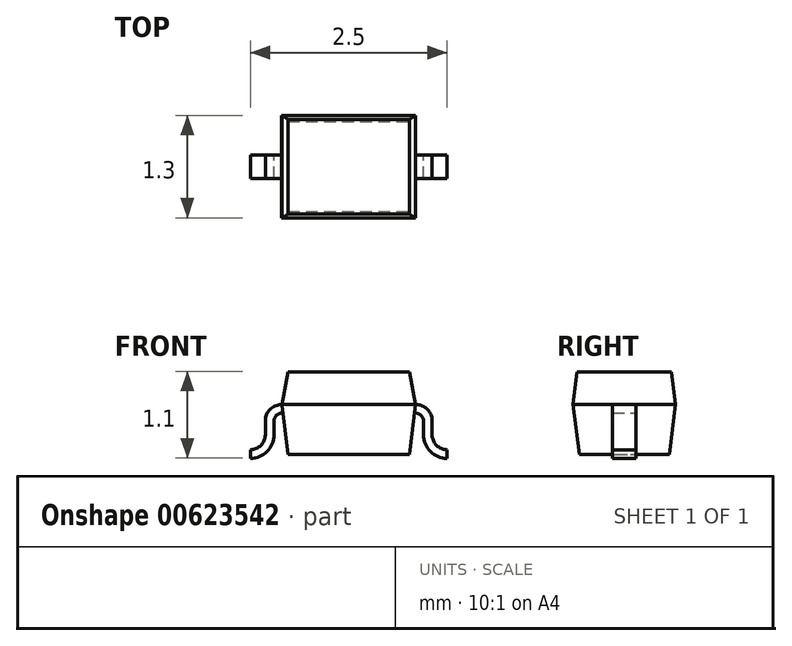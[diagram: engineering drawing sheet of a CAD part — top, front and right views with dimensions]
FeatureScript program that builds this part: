
annotation { "Feature Type Name" : "Feature", "Feature Type Description" : "" }
export const myFeature = defineFeature(function(context is Context, id is Id, definition is map)
    precondition{}
    {
        {
            var Q0;
            Q0=qCreatedBy(makeId("Front.planeOp"),FACE);
            var sketch = newSketch(context, id + "F0", { "sketchPlane" : qUnion([Q0])});
            skPoint(sketch, "E0.middle", {"position": v(0, 0) * mm});
            skLineSegment(sketch, "E1", {"start": v(1.25, -0.57) * mm, "end": v(1.25, -0.57) * mm});
            skLineSegment(sketch, "E2", {"start": v(1.25, -0.57) * mm, "end": v(1.25, -0.46) * mm});
            skLineSegment(sketch, "E3", {"start": v(1.25, -0.46) * mm, "end": v(1.25, -0.46) * mm});
            skLineSegment(sketch, "E4", {"start": v(1.06, -0.27) * mm, "end": v(1.06, -0.09) * mm});
            skLineSegment(sketch, "E5", {"start": v(-0.95, -0.1) * mm, "end": v(-0.95, -0.27) * mm});
            skLineSegment(sketch, "E6", {"start": v(-1.25, -0.57) * mm, "end": v(-1.25, -0.57) * mm});
            skLineSegment(sketch, "E7", {"start": v(-1.25, -0.57) * mm, "end": v(-1.25, -0.46) * mm});
            skLineSegment(sketch, "E8", {"start": v(-1.25, -0.46) * mm, "end": v(-1.25, -0.46) * mm});
            skLineSegment(sketch, "E9", {"start": v(-1.06, -0.27) * mm, "end": v(-1.06, -0.1) * mm});
            skLineSegment(sketch, "E10", {"start": v(-0.85, 0.11) * mm, "end": v(-0.85, 0.11) * mm});
            skLineSegment(sketch, "E11", {"start": v(-0.85, 0.11) * mm, "end": v(-0.77, -0.52) * mm});
            skLineSegment(sketch, "E12", {"start": v(-0.85, 0) * mm, "end": v(-0.84, 0) * mm});
            skPoint(sketch, "E13.visualSharp", {"position": v(1.06, -0.46) * mm});
            skArc(sketch, "E13.filletArc", {"start": v(1.06, -0.27) * mm, "mid": v(1.12, -0.4) * mm, "end": v(1.25, -0.46) * mm});
            skPoint(sketch, "E14.visualSharp", {"position": v(0.95, -0.57) * mm});
            skArc(sketch, "E14.filletArc", {"start": v(0.95, -0.28) * mm, "mid": v(1.04, -0.49) * mm, "end": v(1.25, -0.57) * mm});
            skPoint(sketch, "E15.visualSharp", {"position": v(-1.06, 0.11) * mm});
            skArc(sketch, "E15.filletArc", {"start": v(-0.85, 0.11) * mm, "mid": v(-1, 0.05) * mm, "end": v(-1.06, -0.1) * mm});
            skPoint(sketch, "E16.visualSharp", {"position": v(-0.95, 0) * mm});
            skArc(sketch, "E16.filletArc", {"start": v(-0.85, 0) * mm, "mid": v(-0.92, -0.03) * mm, "end": v(-0.95, -0.1) * mm});
            skPoint(sketch, "E17.visualSharp", {"position": v(-0.95, -0.57) * mm});
            skArc(sketch, "E17.filletArc", {"start": v(-1.25, -0.57) * mm, "mid": v(-1.04, -0.49) * mm, "end": v(-0.95, -0.27) * mm});
            skPoint(sketch, "E18.visualSharp", {"position": v(-1.06, -0.46) * mm});
            skArc(sketch, "E18.filletArc", {"start": v(-1.25, -0.46) * mm, "mid": v(-1.12, -0.4) * mm, "end": v(-1.06, -0.27) * mm});
            skLineSegment(sketch, "E19", {"start": v(0.85, 0) * mm, "end": v(0.84, 0) * mm});
            skLineSegment(sketch, "E20", {"start": v(0.95, -0.27) * mm, "end": v(0.95, -0.1) * mm});
            skLineSegment(sketch, "E21", {"start": v(1.06, -0.1) * mm, "end": v(1.06, -0.09) * mm});
            skLineSegment(sketch, "E22", {"start": v(-0.85, 0.11) * mm, "end": v(0.85, 0.11) * mm});
            skLineSegment(sketch, "E23", {"start": v(-0.77, -0.52) * mm, "end": v(0.77, -0.52) * mm});
            skLineSegment(sketch, "E24", {"start": v(0.77, -0.52) * mm, "end": v(0.85, 0.11) * mm});
            skLineSegment(sketch, "E25", {"start": v(-0.77, 0.53) * mm, "end": v(-0.85, 0.11) * mm});
            skLineSegment(sketch, "E26", {"start": v(-0.77, 0.53) * mm, "end": v(0.77, 0.53) * mm});
            skLineSegment(sketch, "E27", {"start": v(0.77, 0.53) * mm, "end": v(0.85, 0.11) * mm});
            skLineSegment(sketch, "E28", {"start": v(0.85, 0.11) * mm, "end": v(0.85, 0.11) * mm});
            skPoint(sketch, "E29.visualSharp", {"position": v(0.95, 0) * mm});
            skArc(sketch, "E29.filletArc", {"start": v(0.95, -0.1) * mm, "mid": v(0.92, -0.03) * mm, "end": v(0.85, 0) * mm});
            skPoint(sketch, "E30.visualSharp", {"position": v(1.06, 0.11) * mm});
            skArc(sketch, "E30.filletArc", {"start": v(1.06, -0.1) * mm, "mid": v(1, 0.05) * mm, "end": v(0.85, 0.11) * mm});
            skSolve(sketch);
        }
        {
            var Q0;
            Q0=makeQuery(id+"F0.imprint","IMPRINT",FACE,{"disambiguationData":[TD([[makeQuery(id+"F0.imprint","IMPRINT",EDGE,{"derivedFrom":sQuery(id+"F0.wireOp",EDGE,"E22")}),1.0]])]});
            var Q1;
            {var subQ0=sQuery(id+"F0.wireOp",EDGE,"E22");Q1=makeQuery(id+"F0.imprint","IMPRINT",FACE,{"disambiguationData":[TD([[makeQuery(id+"F0.imprint","IMPRINT",EDGE,{"derivedFrom":subQ0}),-1.0]])]});}
            extrude(context, id + "F1", {"entities" : qUnion([Q0, Q1]), "endBound" : BoundingType.SYMMETRIC, "depth" : 1.3 * mm, "offsetDistance" : 25 * mm});
        }
        {
            var Q0;
            Q0=makeQuery(id+"F0.imprint","IMPRINT",FACE,{"disambiguationData":[TD([[makeQuery(id+"F0.imprint","IMPRINT",EDGE,{"derivedFrom":sQuery(id+"F0.wireOp",EDGE,"E5")}),-1.0]])]});
            var Q1;
            Q1=makeQuery(id+"F0.imprint","IMPRINT",FACE,{"disambiguationData":[TD([[makeQuery(id+"F0.imprint","IMPRINT",EDGE,{"derivedFrom":sQuery(id+"F0.wireOp",EDGE,"E2")}),1.0]])]});
            extrude(context, id + "F2", {"entities" : qUnion([Q0, Q1]), "endBound" : BoundingType.SYMMETRIC, "depth" : 0.3 * mm, "offsetDistance" : 25 * mm});
        }
        {
            var Q0;
            Q0=qCreatedBy(makeId("Right.planeOp"),FACE);
            var sketch = newSketch(context, id + "F3", { "sketchPlane" : qUnion([Q0])});
            skLineSegment(sketch, "E31", {"start": v(0.65, 0.1) * mm, "end": v(-0.65, 0.1) * mm});
            skLineSegment(sketch, "E32", {"start": v(-0.65, 0.1) * mm, "end": v(-0.65, 0.53) * mm});
            skLineSegment(sketch, "E33", {"start": v(0.65, 0.11) * mm, "end": v(0.65, 0.53) * mm});
            skLineSegment(sketch, "E34", {"start": v(-0.65, 0.53) * mm, "end": v(-0.6, 0.53) * mm});
            skLineSegment(sketch, "E35", {"start": v(-0.6, 0.53) * mm, "end": v(-0.65, 0.1) * mm});
            skLineSegment(sketch, "E36", {"start": v(0.65, 0.53) * mm, "end": v(0.6, 0.53) * mm});
            skLineSegment(sketch, "E37", {"start": v(0.6, 0.53) * mm, "end": v(0.65, 0.11) * mm});
            skLineSegment(sketch, "E38", {"start": v(-0.65, 0.1) * mm, "end": v(-0.65, -0.52) * mm});
            skLineSegment(sketch, "E39", {"start": v(0.65, 0.1) * mm, "end": v(0.65, -0.52) * mm});
            skLineSegment(sketch, "E40", {"start": v(-0.65, 0.1) * mm, "end": v(-0.57, -0.52) * mm});
            skLineSegment(sketch, "E41", {"start": v(-0.57, -0.52) * mm, "end": v(-0.65, -0.52) * mm});
            skLineSegment(sketch, "E42", {"start": v(0.65, 0.1) * mm, "end": v(0.57, -0.52) * mm});
            skLineSegment(sketch, "E43", {"start": v(0.57, -0.52) * mm, "end": v(0.65, -0.52) * mm});
            skSolve(sketch);
        }
        {
            var Q0;
            Q0=makeQuery(id+"F3.imprint","IMPRINT",FACE,{"disambiguationData":[TD([[makeQuery(id+"F3.imprint","IMPRINT",EDGE,{"derivedFrom":sQuery(id+"F3.wireOp",EDGE,"E33")}),1.0]])]});
            var Q1;
            Q1=makeQuery(id+"F3.imprint","IMPRINT",FACE,{"disambiguationData":[TD([[makeQuery(id+"F3.imprint","IMPRINT",EDGE,{"derivedFrom":sQuery(id+"F3.wireOp",EDGE,"E39")}),-1.0]])]});
            var Q2;
            Q2=makeQuery(id+"F3.imprint","IMPRINT",FACE,{"disambiguationData":[TD([[makeQuery(id+"F3.imprint","IMPRINT",EDGE,{"derivedFrom":sQuery(id+"F3.wireOp",EDGE,"E38")}),1.0]])]});
            var Q3;
            Q3=makeQuery(id+"F3.imprint","IMPRINT",FACE,{"disambiguationData":[TD([[makeQuery(id+"F3.imprint","IMPRINT",EDGE,{"derivedFrom":sQuery(id+"F3.wireOp",EDGE,"E32")}),-1.0]])]});
            extrude(context, id + "F4", {"entities" : qUnion([Q0, Q1, Q2, Q3]), "operationType" : NewBodyOperationType.REMOVE, "endBound" : BoundingType.SYMMETRIC, "oppositeDirection" : true, "depth" : 1.7 * mm, "offsetDistance" : 25 * mm});
        }
    });
